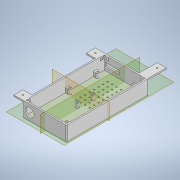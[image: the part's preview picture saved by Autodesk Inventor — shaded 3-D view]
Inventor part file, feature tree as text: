
AUTODESK INVENTOR PART (.ipt)
format: ipt  version: 2022 (Build 260153000, 153)  size: 408,576 bytes
history: native  units: in
note: dims shown in document units (in); Inventor stores cm internally (conversion verified against a paired STEP export)
features: reference x13, extrude x11, sketch x11, projected_geometry x5, other x5, plane x3, mirror x2, pattern_linear x1, hole x1, chamfer x1, fillet x1
ambient origin geometry x8: Origin, YZ Plane, XZ Plane, XY Plane, X Axis, Y Axis, Z Axis, Center Point
bodies: Body1 (feature_tree)
feature tree (54):
  plane  "Work Plane2"
  extrude  "Extrusion14"  Depth=0.7874in
  extrude  "Extrusion15"  Depth=0.1181in TaperAngle=0.0deg
  extrude  "Extrusion17"  Depth=1.1811in TaperAngle=0.0deg
  extrude  "Extrusion18"  Depth=0.1575in
  extrude  "Extrusion19"  Depth=0.3937in TaperAngle=0.0deg
  pattern_linear  "Rectangular Pattern1"  Count1=8 Spacing1=0.3937in
  extrude  "Extrusion20"  Depth=0.7874in
  extrude  "Extrusion21"  Depth=0.7874in
  extrude  "Extrusion22"  Depth=0.3937in TaperAngle=0.0deg
  extrude  "Extrusion23"  Depth=0.0787in
  hole  "Hole19"  [1 undecoded]
  sketch  "Sketch32"  dims[d136=1.9685in d138=0.3937in d139=0.5906in d140=0.7874in d141=0.3937in d142=0.0in d143=0.0787in d144=0.0787in d145=0.0787in d146=0.0787in d147=0.3937in d148=0.0in d149=0.3937in d150=0.0in d151=1.5748in d152=0.1181in d153=0.0in d154=0.126in d155=0.2362in d156=0.119in d157=0.0787in d158=0.563in d159=0.315in d160=0.8108in d161=0.1969in d162=0.0787in d163=0.0787in d164=0.0in d165=0.0689in d166=0.0in d170=0.2236in d171=0.0787in d172=45.0deg d173=0.0787in d174=0.7874in]
  extrude  "Extrusion24"  Depth=0.0787in
  extrude  "Extrusion25"  Depth=0.0787in
  plane  "Work Plane3"
  plane  "Work Plane4"
  mirror  "Mirror1"
  mirror  "Mirror2"
  chamfer  "Chamfer2"  Distance=0.3937in
  fillet  "Fillet2"  Radius=0.3937in
  sketch  "Sketch22"  dims[d108=0.2756in d109=0.7874in]
  reference  "Reference1"
  reference  "Reference2"
  reference  "Reference3"
  sketch  "Sketch23"  dims[d111=0.7874in d112=0.1181in d113=0.0in]
  projected_geometry  "Projected Loop2"
  sketch  "Sketch24"  dims[d114=0.1181in d115=1.1811in d116=0.0in]
  reference  "Reference4"
  reference  "Reference5"
  reference  "Reference6"
  reference  "Reference7"
  reference  "Reference8"
  sketch  "Sketch25"  dims[d117=0.1969in d122=0.1575in]
  projected_geometry  "Projected Loop3"
  sketch  "Sketch26"  dims[d123=0.315in d124=0.3937in d125=0.0in]
  sketch  "Sketch27"  dims[d126=0.1575in d127=0.0in]
  projected_geometry  "Projected Loop4"
  sketch  "Sketch28"  dims[d128=0.1181in]
  reference  "Reference9"
  reference  "Reference10"
  reference  "Reference11"
  reference  "Reference12"
  reference  "Reference13"
  sketch  "Sketch29"  dims[d129=0.7283in]
  projected_geometry  "Projected Loop5"
  sketch  "Sketch30"  dims[d130=0.9843in]
  sketch  "Sketch31"  dims[d131=0.3937in d132=0.0in d133=3.1496in d135=0.3937in]
  projected_geometry  "Projected Loop6"
  parser-record x1  (decoder bookkeeping rows leaked as tree rows — omitted from the tree; the rows remain in map.json)
  other  "Electronics Box.iam"
  other  "SKR MINI E3 V1.2:1"
  other  "SSR-40:1"
  other  "SKR Mini E3 v2.0:1"
note: 1 required parameter value undecoded (feature->parameter linkage not recoverable at this tier; creation-order binding heuristic only, values carry confidence <= 0.55)
note: 1 file-system path scrubbed to <path> (originals preserved in map.json)
